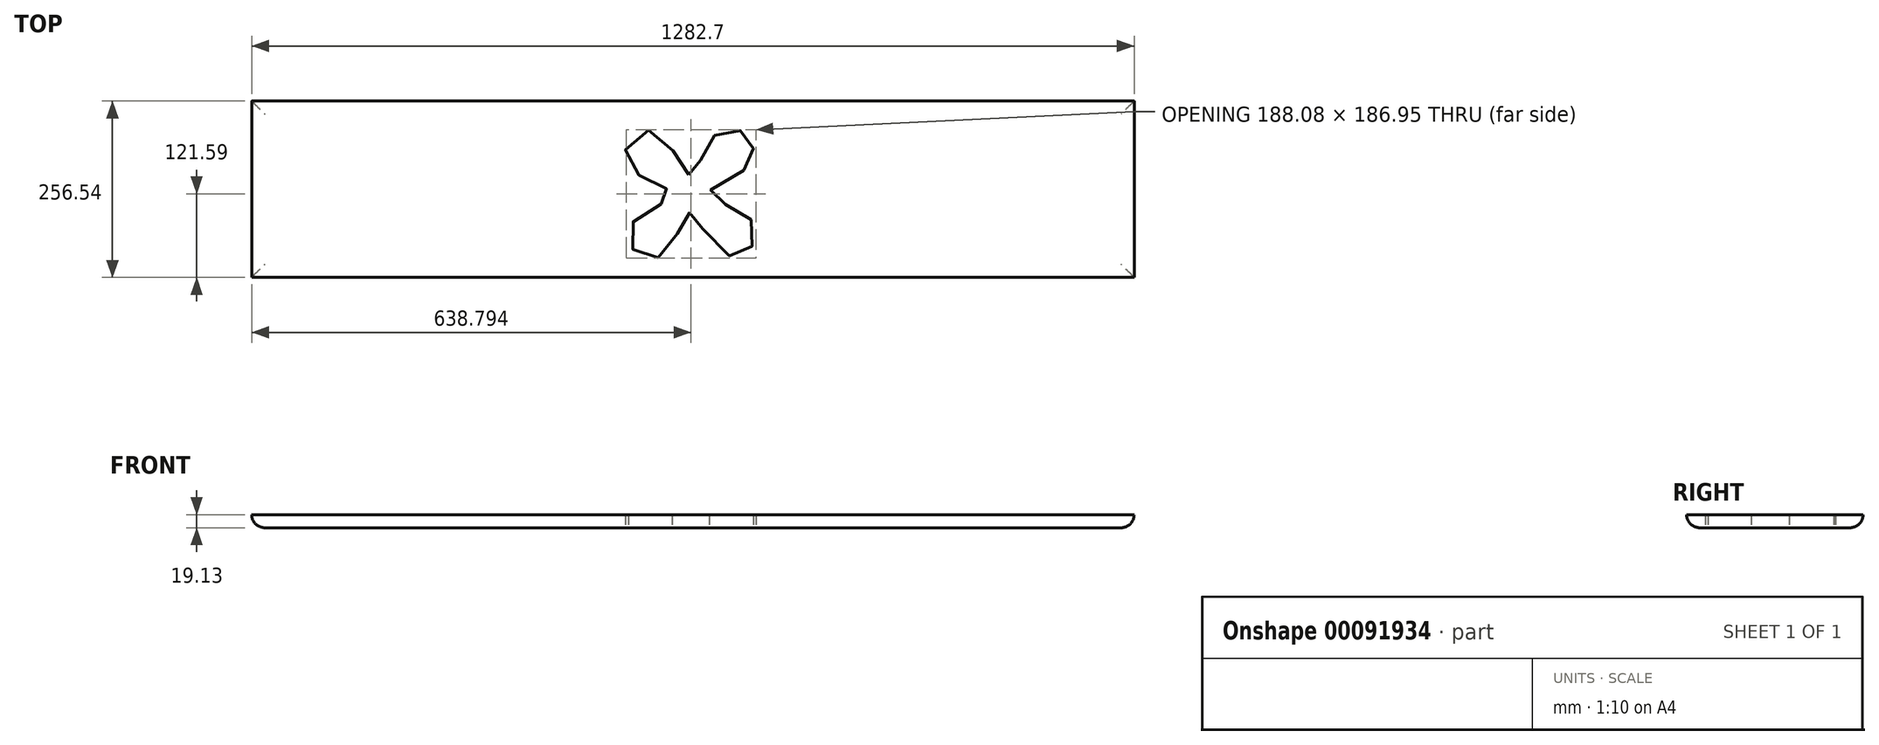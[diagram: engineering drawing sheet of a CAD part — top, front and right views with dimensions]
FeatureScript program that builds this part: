
annotation { "Feature Type Name" : "Feature", "Feature Type Description" : "" }
export const myFeature = defineFeature(function(context is Context, id is Id, definition is map)
    precondition{}
    {
        {
            var Q0;
            Q0=qCreatedBy(makeId("Top.planeOp"),FACE);
            var sketch = newSketch(context, id + "F0", { "sketchPlane" : qUnion([Q0])});
            skLineSegment(sketch, "E0.bottom", {"start": v(-639.45, 48.8) * mm, "end": v(643.25, 48.8) * mm});
            skLineSegment(sketch, "E0.top", {"start": v(-639.45, -207.75) * mm, "end": v(643.25, -207.75) * mm});
            skLineSegment(sketch, "E0.left", {"start": v(-639.45, 48.8) * mm, "end": v(-639.45, -207.75) * mm});
            skLineSegment(sketch, "E0.right", {"start": v(643.25, 48.8) * mm, "end": v(643.25, -207.75) * mm});
            skSolve(sketch);
        }
        {
            var Q0;
            Q0 = qSketchRegion(id + "F0", true);
            extrude(context, id + "F1", {"entities" : qUnion([Q0]), "depth" : 19.13 * mm});
        }
        {
            var Q0;
            Q0=makeQuery(id+"F1.opExtrude","CAP_EDGE",EDGE,{"disambiguationData":[OSD([sQuery(id+"F0.wireOp",EDGE,"E0.top")])],"isStart":true});
            var Q1;
            Q1=makeQuery(id+"F1.opExtrude","CAP_EDGE",EDGE,{"disambiguationData":[OSD([sQuery(id+"F0.wireOp",EDGE,"E0.left")])],"isStart":true});
            var Q2;
            Q2=makeQuery(id+"F1.opExtrude","CAP_EDGE",EDGE,{"disambiguationData":[OSD([sQuery(id+"F0.wireOp",EDGE,"E0.bottom")])],"isStart":true});
            var Q3;
            Q3=makeQuery(id+"F1.opExtrude","CAP_EDGE",EDGE,{"disambiguationData":[OSD([sQuery(id+"F0.wireOp",EDGE,"E0.right")])],"isStart":true});
            fillet(context, id + "F2", {"entities" : qUnion([Q0, Q1, Q2, Q3]), "radius" : 19.06 * mm, "tangentPropagation" : true, "allowEdgeOverflow" : false});
        }
        {
            var Q0;
            Q0=makeQuery(id+"F1.opExtrude","CAP_EDGE",EDGE,{"disambiguationData":[OSD([sQuery(id+"F0.wireOp",EDGE,"E0.bottom")])],"isStart":false});
            var Q1;
            Q1=makeQuery(id+"F1.opExtrude","CAP_EDGE",EDGE,{"disambiguationData":[OSD([sQuery(id+"F0.wireOp",EDGE,"E0.left")])],"isStart":false});
            var Q2;
            {var subQ0=sQuery(id+"F0.wireOp",EDGE,"E0.top");Q2=makeQuery(id+"F2.opFillet","BLEND_EDGE",EDGE,{"blendedFrom":[makeQuery(id+"F1.opExtrude","CAP_EDGE",EDGE,{"disambiguationData":[OSD([subQ0])],"isStart":true}),makeQuery(id+"F1.opExtrude","SWEPT_FACE",FACE,{"disambiguationData":[OSD([subQ0])]})],"blendedInto":[makeQuery(id+"F1.opExtrude","SWEPT_FACE",FACE,{"disambiguationData":[OSD([subQ0])]})]});}
            var Q3;
            Q3=makeQuery(id+"F1.opExtrude","CAP_EDGE",EDGE,{"disambiguationData":[OSD([sQuery(id+"F0.wireOp",EDGE,"E0.right")])],"isStart":false});
            var Q4;
            Q4=makeQuery(id+"F1.opExtrude","CAP_EDGE",EDGE,{"disambiguationData":[OSD([sQuery(id+"F0.wireOp",EDGE,"E0.top")])],"isStart":false});
            fillet(context, id + "F3", {"entities" : qUnion([Q0, Q1, Q2, Q3, Q4]), "radius" : 25.4 * mm, "tangentPropagation" : true, "allowEdgeOverflow" : false});
        }
        {
            var Q0;
            Q0=makeQuery(id+"F1.opExtrude","CAP_FACE",FACE,{"disambiguationData":[OSD([sQuery(id+"F0.wireOp",EDGE,"E0.bottom"),sQuery(id+"F0.wireOp",EDGE,"E0.top"),sQuery(id+"F0.wireOp",EDGE,"E0.left"),sQuery(id+"F0.wireOp",EDGE,"E0.right")])],"isStart":false});
            var sketch = newSketch(context, id + "F4", { "sketchPlane" : qUnion([Q0])});
            skSolve(sketch);
        }
        {
            var Q0;
            {var subQ0=sQuery(id+"F0.wireOp",EDGE,"E0.right");var subQ1=sQuery(id+"F0.wireOp",EDGE,"E0.left");var subQ2=sQuery(id+"F0.wireOp",EDGE,"E0.top");var subQ3=sQuery(id+"F0.wireOp",EDGE,"E0.bottom");var subQ4=makeQuery(id+"F1.opExtrude","CAP_FACE",FACE,{"disambiguationData":[OSD([subQ3,subQ2,subQ1,subQ0])],"isStart":false});Q0=makeQuery(id+"F4.imprint","IMPRINT",FACE,{"disambiguationData":[TD([[makeQuery(id+"F4.imprint","IMPRINT",EDGE,{"derivedFrom":makeQuery(id+"F3.opFillet","BLEND_EDGE",EDGE,{"blendedFrom":[makeQuery(id+"F1.opExtrude","CAP_EDGE",EDGE,{"disambiguationData":[OSD([subQ3])],"isStart":false}),subQ4],"blendedInto":[subQ4]})}),1.0]])]});}
            var sketch = newSketch(context, id + "F5", { "sketchPlane" : qUnion([Q0])});
            skFitSpline(sketch, "E1", {"points": [v(-3.95, -58.34) * mm, v(-10.76, -51.53) * mm, v(-26, -24.95) * mm, v(-44.47, 0) * mm, v(-71.37, 5.51) * mm, v(-92.77, -11.66) * mm, v(-94.71, -37.27) * mm, v(-80.77, -56.4) * mm, v(-61, -65.15) * mm, v(-36.37, -78.76) * mm, v(-30.2, -82.65) * mm, v(-28.91, -89.13) * mm, v(-57.22, -107.71) * mm, v(-79.78, -121.36) * mm, v(-90.77, -138.41) * mm, v(-88.32, -162.4) * mm, v(-74.69, -175.75) * mm, v(-53.97, -180.11) * mm, v(-32.71, -167.3) * mm, v(-20.72, -143.6) * mm, v(-9.27, -121.79) * mm, v(-4.91, -114.97) * mm, v(0, -113.6) * mm, v(4.9, -116.33) * mm, v(11.17, -127.5) * mm, v(38.97, -170.03) * mm, v(60.23, -176.57) * mm, v(74.4, -174.66) * mm, v(90.21, -159.13) * mm, v(92.94, -139.77) * mm, v(83.95, -120.97) * mm, v(65.14, -109.8) * mm, v(40.6, -97.53) * mm, v(27.52, -89.62) * mm, v(26.7, -82.26) * mm, v(57.73, -62.04) * mm, v(84, -44.42) * mm, v(89.2, -29.4) * mm, v(89.51, -17.1) * mm, v(83.33, -4) * mm, v(72.05, 5.1) * mm, v(50.22, 8.37) * mm, v(34.58, 0) * mm, v(21.84, -18.91) * mm, v(12.75, -37.83) * mm, v(5.83, -52.02) * mm, v(0, -58.2) * mm, v(-3.95, -58.34) * mm]});
            skSolve(sketch);
        }
        {
            var Q0;
            Q0 = qSketchRegion(id + "F5", true);
            extrude(context, id + "F6", {"entities" : qUnion([Q0]), "operationType" : NewBodyOperationType.REMOVE, "oppositeDirection" : true, "depth" : 219.28 * mm});
        }
    });
